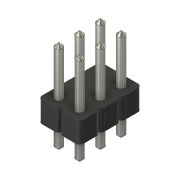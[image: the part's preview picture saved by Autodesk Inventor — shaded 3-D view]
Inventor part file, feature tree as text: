
AUTODESK INVENTOR PART (.ipt)
format: ipt  version: 2020 (Build 240168000, 168)  size: 210,944 bytes
history: native  units: in
note: dims shown in document units (in); Inventor stores cm internally (conversion verified against a paired STEP export)
features: extrude x2, sketch x2, chamfer x1
ambient origin geometry x8: Origin, YZ Plane, XZ Plane, XY Plane, X Axis, Y Axis, Z Axis, Center Point
bodies: Solid1 (feature_tree)
feature tree (5):
  extrude  "Extrusion1"  Depth=0.1in
  extrude  "Extrusion2"  Depth=0.23in TaperAngle=0.0deg
  chamfer  "Chamfer1"  Distance=0.015in Angle=45.0deg
  sketch  "Sketch1"  dims[d0=0.1in d1=0.0in d2=0.035in]
  sketch  "Sketch2"  dims[d3=0.7874in d5=0.1in d6=1.1811in d8=0.1in d11=0.23in d12=0.214in d13=0.0in d14=0.0in d15=0.015in d16=0.125in d17=45.0deg]
